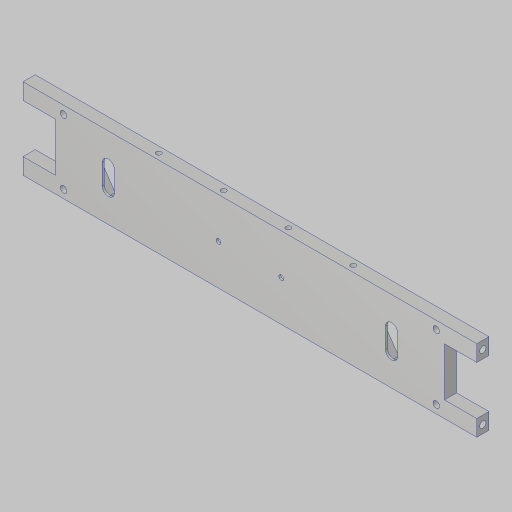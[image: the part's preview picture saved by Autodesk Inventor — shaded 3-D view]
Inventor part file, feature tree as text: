
AUTODESK INVENTOR PART (.ipt)
format: ipt  version: 2023.5 (Build 275446000, 446)  size: 491,520 bytes
history: native  units: in
note: dims shown in document units (in); Inventor stores cm internally (conversion verified against a paired STEP export)
features: sketch x9, hole x5, extrude x4, projected_geometry x3, fillet x1
ambient origin geometry x8: Origin, YZ Plane, XZ Plane, XY Plane, X Axis, Y Axis, Z Axis, Center Point
bodies: Solid1 (feature_tree)
feature tree (22):
  extrude  "Extrusion1"  Depth=2.5in
  hole  "Hole3"  [1 undecoded]
  hole  "Hole4"  [1 undecoded]
  extrude  "Extrusion3"  Depth=0.375in
  extrude  "Extrusion4"  Depth=0.5in
  sketch  "Sketch10"  dims[d49=1.0in d50=1.5in d52=0.5in]
  extrude  "Extrusion5"  Depth=1.5in
  fillet  "Fillet1"  Radius=0.5in
  hole  "Hole6"  [1 undecoded]
  hole  "Hole7"  [1 undecoded]
  hole  "Hole8"  [1 undecoded]
  sketch  "Sketch1"  dims[d0=14.0in d1=2.5in]
  sketch  "Sketch5"  dims[d2=0.375in d3=0.0in d29=2.0in]
  sketch  "Sketch6"  dims[d30=0.196in d31=0.5in d32=0.385in d33=0.25in d34=0.5635in d35=1.0in d36=0.8108in d37=2.0in]
  sketch  "Sketch8"  dims[d38=0.156in d39=0.38in d40=0.375in d41=0.25in d42=0.5635in d43=0.536in d44=0.8108in d45=1.0in]
  sketch  "Sketch9"  dims[d46=1.5in d47=0.5in]
  projected_geometry  "Projected Loop1"
  projected_geometry  "Projected Loop2"
  sketch  "Sketch11"  dims[d53=1.5625in d54=0.0in d55=0.375in]
  projected_geometry  "Projected Loop3"
  sketch  "Sketch12"  dims[d56=1.0in d57=2.63in]
  sketch  "Sketch13"  dims[d58=0.0in d59=0.0in d60=4.0in d61=2.0in d69=0.25in d72=0.0625in d73=0.0625in d74=0.0625in d75=0.0625in d76=0.0625in d77=0.0625in d78=0.3125in d79=0.0in d80=0.1875in d81=1.6202in d82=0.156in d83=0.38in d84=0.375in d85=0.25in d86=0.5635in d87=1.0in d88=0.8108in d89=1.25in d90=1.25in d91=0.201in d92=0.75in d93=0.385in d94=0.25in d95=0.5635in d96=1.0in d97=0.8108in d98=1.9366in d99=0.15in d100=0.75in d101=0.279in d102=0.25in d103=0.5635in d104=1.0in d105=0.8108in]
note: 5 required parameter values undecoded (feature->parameter linkage not recoverable at this tier; creation-order binding heuristic only, values carry confidence <= 0.55)
